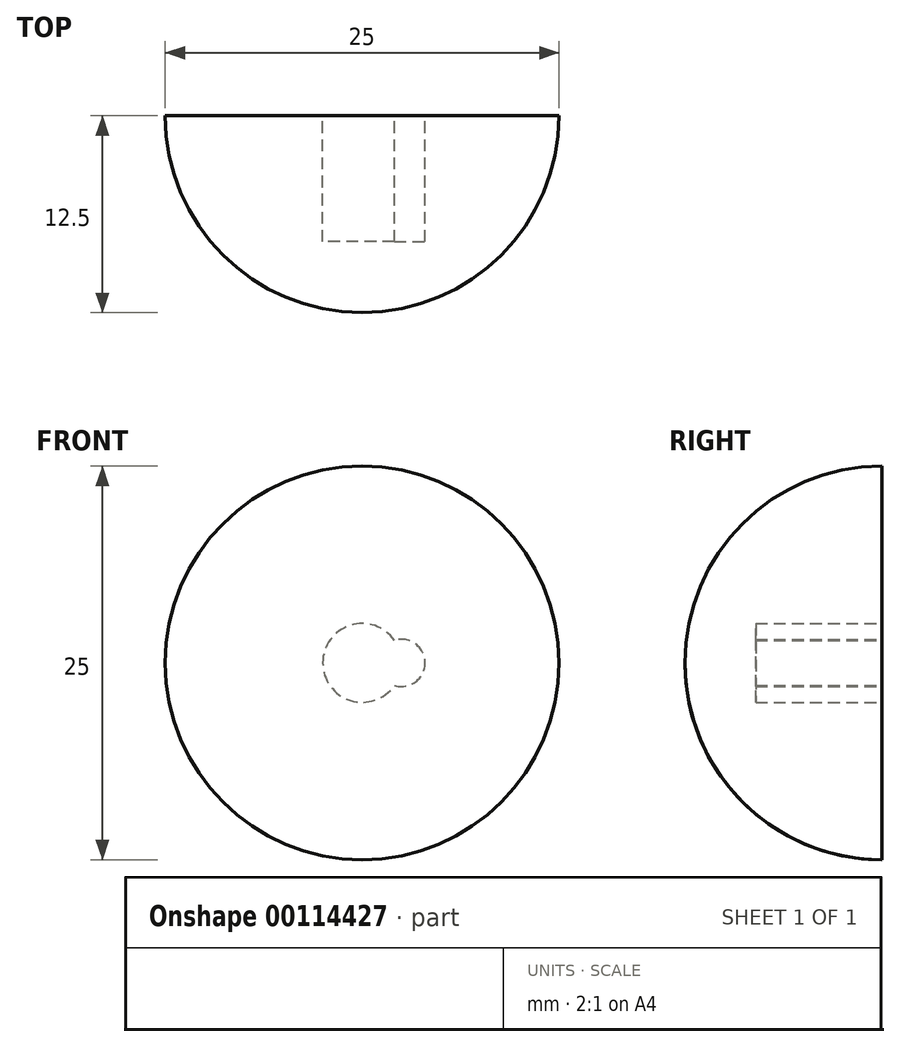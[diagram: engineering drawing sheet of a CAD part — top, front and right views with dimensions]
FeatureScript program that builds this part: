
annotation { "Feature Type Name" : "Feature", "Feature Type Description" : "" }
export const myFeature = defineFeature(function(context is Context, id is Id, definition is map)
    precondition{}
    {
        {
            var Q0;
            Q0=qCreatedBy(makeId("Front.planeOp"),FACE);
            var sketch = newSketch(context, id + "F0", { "sketchPlane" : qUnion([Q0])});
            skCircle(sketch, "E0", {"center": v(0, 0) * mm, "radius": 12.5 * mm});
            skCircle(sketch, "E1", {"center": v(0, 0) * mm, "radius": 2.5 * mm});
            skCircle(sketch, "E2", {"center": v(-1.37, 2.1) * mm, "radius": 1.5 * mm});
            skSolve(sketch);
        }
        {
            var Q0;
            {var subQ0=sQuery(id+"F0.wireOp",EDGE,"E2");var subQ1=sQuery(id+"F0.wireOp",EDGE,"E1");var subQ2=makeQuery(id+"F0.imprint","INTERSECT",VERTEX,{"disambiguationData":[OD(0.0)],"derivedFrom":[subQ1,subQ0]});Q0=makeQuery(id+"F0.imprint","IMPRINT",FACE,{"disambiguationData":[TD([[makeQuery(id+"F0.imprint","IMPRINT",EDGE,{"disambiguationData":[TD([[subQ2,-1.0]])],"derivedFrom":subQ1}),1.0]])]});}
            var Q1;
            {var subQ0=sQuery(id+"F0.wireOp",EDGE,"E2");var subQ1=sQuery(id+"F0.wireOp",EDGE,"E1");var subQ2=makeQuery(id+"F0.imprint","INTERSECT",VERTEX,{"disambiguationData":[OD(0.0)],"derivedFrom":[subQ1,subQ0]});Q1=makeQuery(id+"F0.imprint","IMPRINT",FACE,{"disambiguationData":[TD([[makeQuery(id+"F0.imprint","IMPRINT",EDGE,{"disambiguationData":[TD([[subQ2,1.0]])],"derivedFrom":subQ1}),-1.0]])]});}
            extrude(context, id + "F1", {"entities" : qUnion([Q0, Q1]), "depth" : 8 * mm});
        }
        {
            var Q0;
            Q0=qCreatedBy(makeId("Front.planeOp"),FACE);
            var sketch = newSketch(context, id + "F2", { "sketchPlane" : qUnion([Q0])});
            skCircle(sketch, "E3", {"center": v(0, 0) * mm, "radius": 12.5 * mm});
            skSolve(sketch);
        }
        {
            var Q0;
            Q0 = qSketchRegion(id + "F2", true);
            extrude(context, id + "F3", {"entities" : qUnion([Q0]), "depth" : 12.5 * mm});
        }
        {
            var Q0;
            Q0=makeQuery(id+"F3.opExtrude","CAP_EDGE",EDGE,{"disambiguationData":[OSD([sQuery(id+"F2.wireOp",EDGE,"E3")])],"isStart":false});
            fillet(context, id + "F4", {"entities" : qUnion([Q0]), "radius" : 12.5 * mm, "tangentPropagation" : true, "allowEdgeOverflow" : false});
        }
        {
            var Q0;
            {var subQ0=sQuery(id+"F0.wireOp",EDGE,"E2");var subQ1=sQuery(id+"F0.wireOp",EDGE,"E1");var subQ2=makeQuery(id+"F0.imprint","INTERSECT",VERTEX,{"disambiguationData":[OD(0.0)],"derivedFrom":[subQ1,subQ0]});Q0=makeQuery(id+"F1.opExtrude","SWEPT_BODY",BODY,{"disambiguationData":[OSD([subQ1,subQ0]),TDD([makeQuery(id+"F0.imprint","IMPRINT",EDGE,{"disambiguationData":[TD([[subQ2,-1.0]])],"derivedFrom":subQ1}),makeQuery(id+"F0.imprint","IMPRINT",EDGE,{"disambiguationData":[TD([[subQ2,-1.0]])],"derivedFrom":subQ0})])]});}
            var Q1;
            {var subQ0=sQuery(id+"F0.wireOp",EDGE,"E2");var subQ1=sQuery(id+"F0.wireOp",EDGE,"E1");var subQ2=makeQuery(id+"F0.imprint","INTERSECT",VERTEX,{"disambiguationData":[OD(0.0)],"derivedFrom":[subQ1,subQ0]});Q1=makeQuery(id+"F1.opExtrude","SWEPT_BODY",BODY,{"disambiguationData":[OSD([subQ1,subQ0]),TDD([makeQuery(id+"F0.imprint","IMPRINT",EDGE,{"disambiguationData":[TD([[subQ2,1.0]])],"derivedFrom":subQ1}),makeQuery(id+"F0.imprint","IMPRINT",EDGE,{"disambiguationData":[TD([[subQ2,1.0]])],"derivedFrom":subQ0})])]});}
            deleteBodies(context, id + "F5", {"entities" : qUnion([Q0, Q1])});
        }
        {
            var Q0;
            Q0=qCreatedBy(makeId("Front.planeOp"),FACE);
            var sketch = newSketch(context, id + "F6", { "sketchPlane" : qUnion([Q0])});
            skCircle(sketch, "E4", {"center": v(0, 0) * mm, "radius": 2.5 * mm});
            skCircle(sketch, "E5", {"center": v(2.5, 0) * mm, "radius": 1.5 * mm});
            skSolve(sketch);
        }
        {
            var Q0;
            Q0 = qSketchRegion(id + "F6", true);
            extrude(context, id + "F7", {"entities" : qUnion([Q0]), "operationType" : NewBodyOperationType.REMOVE, "depth" : 8 * mm});
        }
    });
